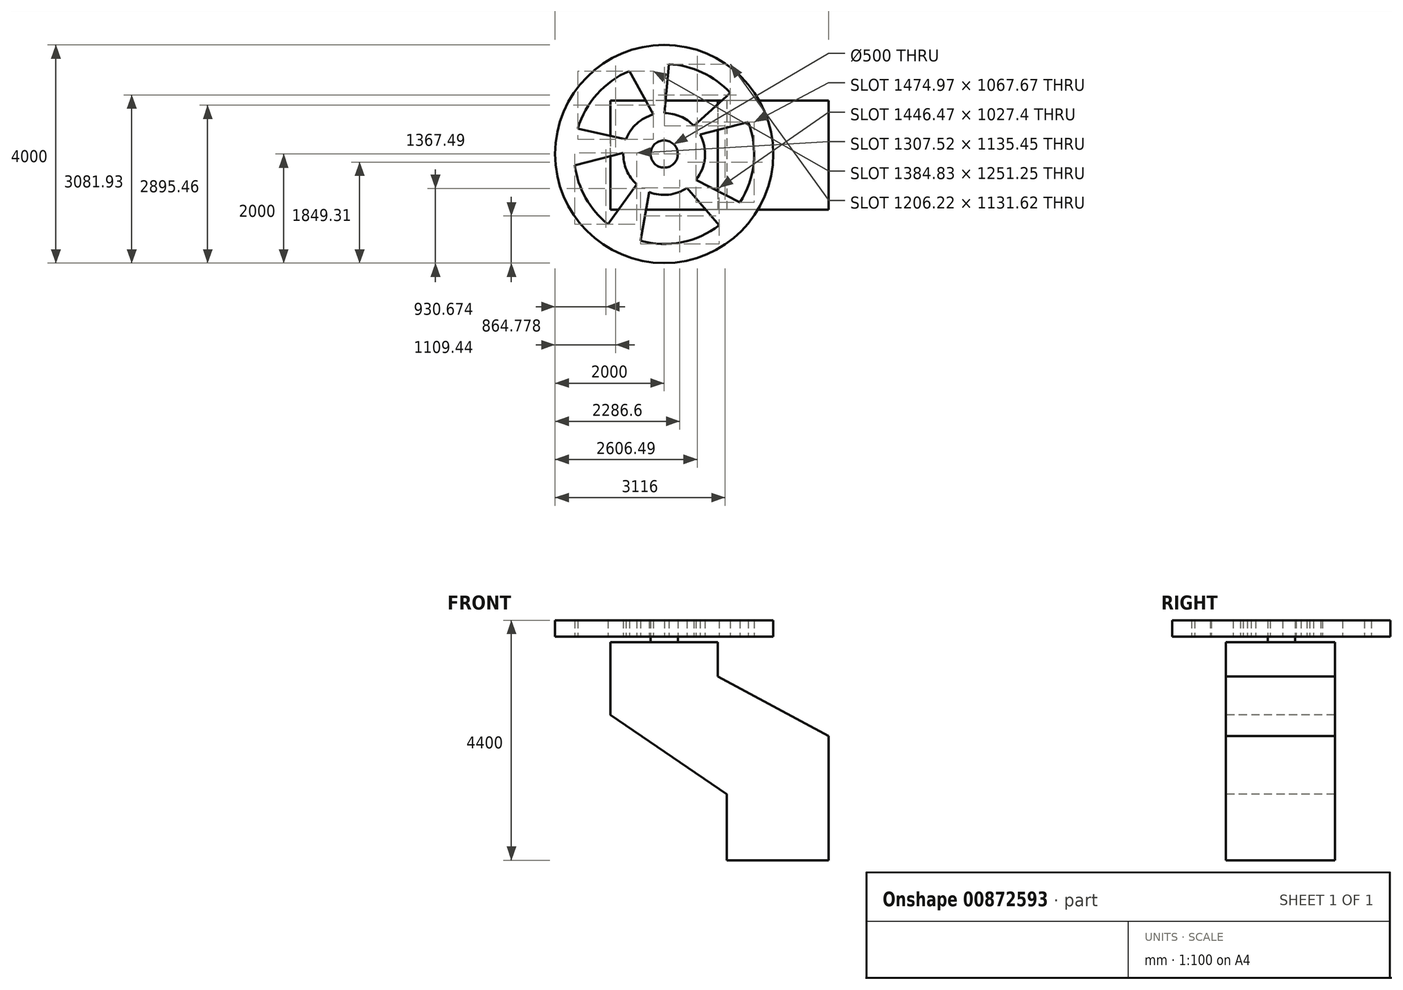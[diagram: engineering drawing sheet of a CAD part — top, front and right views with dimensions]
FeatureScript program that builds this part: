
annotation { "Feature Type Name" : "Feature", "Feature Type Description" : "" }
export const myFeature = defineFeature(function(context is Context, id is Id, definition is map)
    precondition{}
    {
        {
            var Q0;
            Q0=qCreatedBy(makeId("Top.planeOp"),FACE);
            var sketch = newSketch(context, id + "F0", { "sketchPlane" : qUnion([Q0])});
            skLineSegment(sketch, "E0.bottom", {"start": v(0, 0) * mm, "end": v(-4000, 0) * mm});
            skLineSegment(sketch, "E0.top", {"start": v(0, 2000) * mm, "end": v(-4000, 2000) * mm});
            skLineSegment(sketch, "E0.left", {"start": v(0, 0) * mm, "end": v(0, 2000) * mm});
            skLineSegment(sketch, "E0.right", {"start": v(-4000, 0) * mm, "end": v(-4000, 2000) * mm});
            skSolve(sketch);
        }
        {
            var Q0;
            Q0=makeQuery(id+"F0.imprint","IMPRINT",FACE,{"disambiguationData":[TD([[makeQuery(id+"F0.imprint","IMPRINT",EDGE,{"derivedFrom":sQuery(id+"F0.wireOp",EDGE,"E0.bottom")}),-1.0]])]});
            extrude(context, id + "F1", {"entities" : qUnion([Q0]), "depth" : 4000 * mm, "offsetDistance" : 25 * mm});
        }
        {
            var Q0;
            Q0=makeQuery(id+"F1.opExtrude","SWEPT_FACE",FACE,{"disambiguationData":[OSD([sQuery(id+"F0.wireOp",EDGE,"E0.bottom")])]});
            var sketch = newSketch(context, id + "F2", { "sketchPlane" : qUnion([Q0])});
            skLineSegment(sketch, "E1", {"start": v(-1867.6, 0) * mm, "end": v(-1867.6, 1212.97) * mm});
            skLineSegment(sketch, "E2", {"start": v(-1867.6, 1212.97) * mm, "end": v(-4000, 2664.55) * mm});
            skLineSegment(sketch, "E3", {"start": v(0, 2277.24) * mm, "end": v(-2028.86, 3368.02) * mm});
            skLineSegment(sketch, "E4", {"start": v(-2028.86, 3368.02) * mm, "end": v(-2028.86, 4000) * mm});
            skLineSegment(sketch, "E5", {"start": v(-4071.41, 2664.55) * mm, "end": v(-4437.9, 3946.56) * mm});
            skLineSegment(sketch, "E6", {"start": v(-3878.46, 4520.8) * mm, "end": v(-2028.86, 4000) * mm});
            skLineSegment(sketch, "E7", {"start": v(-1867.6, 0) * mm, "end": v(-701.07, -1136.45) * mm});
            skLineSegment(sketch, "E8", {"start": v(971.16, 155.56) * mm, "end": v(0, 2277.24) * mm});
            skLineSegment(sketch, "E9", {"start": v(-4437.9, 3946.56) * mm, "end": v(-4437.9, 391.73) * mm});
            skLineSegment(sketch, "E10", {"start": v(-4437.9, 391.73) * mm, "end": v(-3059.4, -1376.86) * mm});
            skLineSegment(sketch, "E11", {"start": v(-3059.4, -1376.86) * mm, "end": v(-701.07, -1136.45) * mm});
            skLineSegment(sketch, "E12", {"start": v(971.16, 155.56) * mm, "end": v(971.16, 3445.53) * mm});
            skLineSegment(sketch, "E13", {"start": v(971.16, 3445.53) * mm, "end": v(271.22, 4448.8) * mm});
            skLineSegment(sketch, "E14", {"start": v(271.22, 4448.8) * mm, "end": v(-3878.46, 4520.8) * mm});
            skSolve(sketch);
        }
        {
            var Q0;
            {var subQ0=sQuery(id+"F2.wireOp",EDGE,"E1");Q0=makeQuery(id+"F2.imprint","IMPRINT",FACE,{"disambiguationData":[TD([[makeQuery(id+"F2.imprint","IMPRINT",EDGE,{"derivedFrom":subQ0}),1.0]])]});}
            var Q1;
            {var subQ0=sQuery(id+"F2.wireOp",EDGE,"E3");Q1=makeQuery(id+"F2.imprint","IMPRINT",FACE,{"disambiguationData":[TD([[makeQuery(id+"F2.imprint","IMPRINT",EDGE,{"derivedFrom":subQ0}),-1.0]])]});}
            extrude(context, id + "F3", {"entities" : qUnion([Q0, Q1]), "operationType" : NewBodyOperationType.REMOVE, "endBound" : BoundingType.THROUGH_ALL, "oppositeDirection" : true, "depth" : 25 * mm, "offsetDistance" : 25 * mm});
        }
        {
            var Q0;
            Q0=makeQuery(id+"F1.opExtrude","CAP_FACE",FACE,{"disambiguationData":[OSD([sQuery(id+"F0.wireOp",EDGE,"E0.bottom"),sQuery(id+"F0.wireOp",EDGE,"E0.top"),sQuery(id+"F0.wireOp",EDGE,"E0.left"),sQuery(id+"F0.wireOp",EDGE,"E0.right")])],"isStart":false});
            var sketch = newSketch(context, id + "F4", { "sketchPlane" : qUnion([Q0])});
            skCircle(sketch, "E15", {"center": v(-3014.43, 1021.28) * mm, "radius": 250 * mm});
            skPoint(sketch, "E15.centerSnap0", {"position": v(-3014.43, 2000) * mm});
            skSolve(sketch);
        }
        {
            var Q0;
            Q0=makeQuery(id+"F4.imprint","IMPRINT",FACE,{"disambiguationData":[TD([[makeQuery(id+"F4.imprint","IMPRINT",EDGE,{"derivedFrom":sQuery(id+"F4.wireOp",EDGE,"E15")}),1.0]])]});
            extrude(context, id + "F5", {"entities" : qUnion([Q0]), "operationType" : NewBodyOperationType.ADD, "depth" : 100 * mm, "offsetDistance" : 25 * mm});
        }
        {
            var Q0;
            Q0=makeQuery(id+"F5.opExtrude","CAP_FACE",FACE,{"disambiguationData":[OSD([sQuery(id+"F4.wireOp",EDGE,"E15")])],"isStart":false});
            var sketch = newSketch(context, id + "F6", { "sketchPlane" : qUnion([Q0])});
            skCircle(sketch, "E16", {"center": v(-3014.43, 1021.28) * mm, "radius": 2000 * mm});
            skArc(sketch, "E17", {"start": v(-1804.83, 2143.5) * mm, "mid": v(-2315.2, 2515.8) * mm, "end": v(-2928.08, 2669.02) * mm});
            skArc(sketch, "E18", {"start": v(-2470.26, 1537.4) * mm, "mid": v(-2716.73, 1709.66) * mm, "end": v(-3011.05, 1771.27) * mm});
            skLineSegment(sketch, "E19", {"start": v(-3212.58, 1744.63) * mm, "end": v(-3653.8, 2542.37) * mm});
            skLineSegment(sketch, "E20", {"start": v(-3011.05, 1771.27) * mm, "end": v(-2928.08, 2669.02) * mm});
            skLineSegment(sketch, "E21", {"start": v(-2470.26, 1537.4) * mm, "end": v(-1804.83, 2143.5) * mm});
            skPoint(sketch, "E21.endSnap0", {"position": v(-3433.19, 2143.5) * mm});
            skLineSegment(sketch, "E22", {"start": v(-2354.66, 1377.93) * mm, "end": v(-1472.3, 1608.07) * mm});
            skLineSegment(sketch, "E23", {"start": v(-2432.26, 548.44) * mm, "end": v(-1623.88, 133.1) * mm});
            skLineSegment(sketch, "E24", {"start": v(-2594.66, 399.76) * mm, "end": v(-2004.6, -283.61) * mm});
            skLineSegment(sketch, "E25", {"start": v(-3288.83, 323.28) * mm, "end": v(-3451.07, -569.9) * mm});
            skLineSegment(sketch, "E26", {"start": v(-3516.03, 463.7) * mm, "end": v(-4047.88, -264.99) * mm});
            skLineSegment(sketch, "E27", {"start": v(-3764.13, 1042.53) * mm, "end": v(-4651.48, 814.98) * mm});
            skLineSegment(sketch, "E28", {"start": v(-3714.2, 1291.11) * mm, "end": v(-4597.4, 1486.78) * mm});
            skArc(sketch, "E29.trimOffspring", {"start": v(-3212.58, 1744.63) * mm, "mid": v(-3517.4, 1577.62) * mm, "end": v(-3714.2, 1291.11) * mm});
            skArc(sketch, "E30.trimOffspring", {"start": v(-3764.13, 1042.53) * mm, "mid": v(-3703.78, 725.81) * mm, "end": v(-3516.03, 463.7) * mm});
            skArc(sketch, "E31.trimOffspring", {"start": v(-3653.8, 2542.37) * mm, "mid": v(-4244.58, 2120.93) * mm, "end": v(-4597.4, 1486.78) * mm});
            skArc(sketch, "E32.trimOffspring", {"start": v(-4651.48, 814.98) * mm, "mid": v(-4454.74, 216.28) * mm, "end": v(-4047.88, -264.99) * mm});
            skArc(sketch, "E33.trimOffspring", {"start": v(-3288.83, 323.28) * mm, "mid": v(-2932.3, 275.79) * mm, "end": v(-2594.66, 399.76) * mm});
            skArc(sketch, "E34.trimOffspring", {"start": v(-3451.07, -569.9) * mm, "mid": v(-2694.07, -597.32) * mm, "end": v(-2004.6, -283.61) * mm});
            skArc(sketch, "E35.trimOffspring", {"start": v(-2432.26, 548.44) * mm, "mid": v(-2267.7, 951.42) * mm, "end": v(-2354.66, 1377.93) * mm});
            skArc(sketch, "E36.trimOffspring", {"start": v(-1623.88, 133.1) * mm, "mid": v(-1373.07, 852.6) * mm, "end": v(-1472.3, 1608.07) * mm});
            skSolve(sketch);
        }
        {
            var Q0;
            Q0=makeQuery(id+"F6.imprint","IMPRINT",FACE,{"disambiguationData":[TD([[makeQuery(id+"F6.imprint","IMPRINT",EDGE,{"derivedFrom":sQuery(id+"F6.wireOp",EDGE,"E16")}),1.0]])]});
            extrude(context, id + "F7", {"entities" : qUnion([Q0]), "depth" : 300 * mm, "offsetDistance" : 25 * mm});
        }
    });
